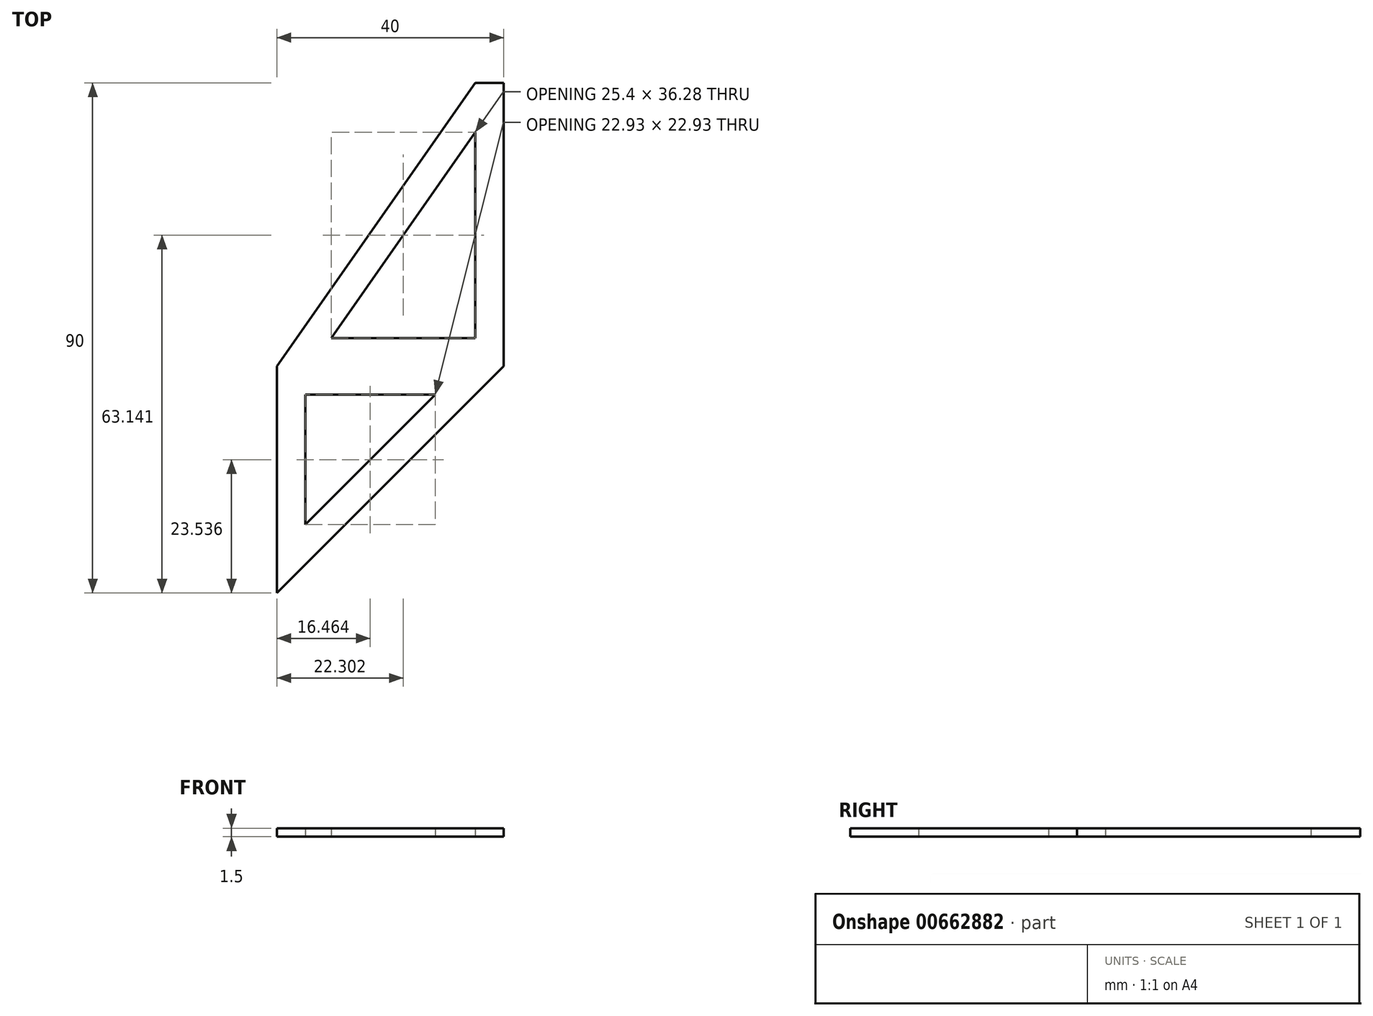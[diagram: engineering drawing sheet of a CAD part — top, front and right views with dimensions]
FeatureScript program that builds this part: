
annotation { "Feature Type Name" : "Feature", "Feature Type Description" : "" }
export const myFeature = defineFeature(function(context is Context, id is Id, definition is map)
    precondition{}
    {
        {
            var Q0;
            Q0=qCreatedBy(makeId("Top.planeOp"),FACE);
            var sketch = newSketch(context, id + "F0", { "sketchPlane" : qUnion([Q0])});
            skLineSegment(sketch, "E0", {"start": v(0, 0) * mm, "end": v(40, 0) * mm});
            skLineSegment(sketch, "E1", {"start": v(40, 0) * mm, "end": v(40, 50) * mm});
            skLineSegment(sketch, "E2", {"start": v(40, 50) * mm, "end": v(35, 50) * mm});
            skLineSegment(sketch, "E3", {"start": v(35, 50) * mm, "end": v(0, 0) * mm});
            skLineSegment(sketch, "E4", {"start": v(0, -40) * mm, "end": v(40, 0) * mm});
            skLineSegment(sketch, "E5", {"start": v(0, 0) * mm, "end": v(0, -40) * mm});
            skLineSegment(sketch, "E6.0", {"start": v(35, 41.28) * mm, "end": v(9.6, 5) * mm});
            skLineSegment(sketch, "E6.1", {"start": v(35, 5) * mm, "end": v(35, 41.28) * mm});
            skLineSegment(sketch, "E6.2", {"start": v(9.6, 5) * mm, "end": v(35, 5) * mm});
            skLineSegment(sketch, "E7.0", {"start": v(5, -5) * mm, "end": v(5, -27.93) * mm});
            skLineSegment(sketch, "E7.1", {"start": v(5, -5) * mm, "end": v(27.93, -5) * mm});
            skLineSegment(sketch, "E7.2", {"start": v(5, -27.93) * mm, "end": v(27.93, -5) * mm});
            skSolve(sketch);
        }
        {
            var Q0;
            Q0=makeQuery(id+"F0.imprint","IMPRINT",FACE,{"disambiguationData":[TD([[makeQuery(id+"F0.imprint","IMPRINT",EDGE,{"derivedFrom":sQuery(id+"F0.wireOp",EDGE,"E0")}),1.0]])]});
            var Q1;
            Q1=makeQuery(id+"F0.imprint","IMPRINT",FACE,{"disambiguationData":[TD([[makeQuery(id+"F0.imprint","IMPRINT",EDGE,{"derivedFrom":sQuery(id+"F0.wireOp",EDGE,"E0")}),-1.0]])]});
            extrude(context, id + "F1", {"entities" : qUnion([Q0, Q1]), "depth" : 1.5 * mm, "offsetDistance" : 25.4 * mm});
        }
    });
